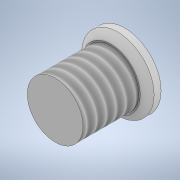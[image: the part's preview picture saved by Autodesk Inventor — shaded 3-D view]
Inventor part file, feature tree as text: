
AUTODESK INVENTOR PART (.ipt)
format: ipt  version: 2021 (Build 250183000, 183)  size: 116,224 bytes
history: native  units: mm
features: extrude x2, sketch x2, thread x1, chamfer x1
ambient origin geometry x8: Origin, YZ Plane, XZ Plane, XY Plane, X Axis, Y Axis, Z Axis, Center Point
bodies: Solid1 (feature_tree)
feature tree (6):
  extrude  "Extrusion1"  Depth=1.0mm TaperAngle=0.0deg
  extrude  "Extrusion2"  Depth=4.0mm TaperAngle=0.0deg
  thread  "Thread1"  [1 undecoded]
  chamfer  "Chamfer2"  Distance=2.0mm Angle=45.0deg
  sketch  "Sketch1"  dims[d0=5.2mm d1=1.0mm d2=0.0mm]
  sketch  "Sketch2"  dims[d3=4.0mm d4=4.0mm d5=0.0mm d6=5.0mm d7=0.0mm d22=0.5mm d23=2.0mm d24=45.0deg]
note: 1 required parameter value undecoded (feature->parameter linkage not recoverable at this tier; creation-order binding heuristic only, values carry confidence <= 0.55)
